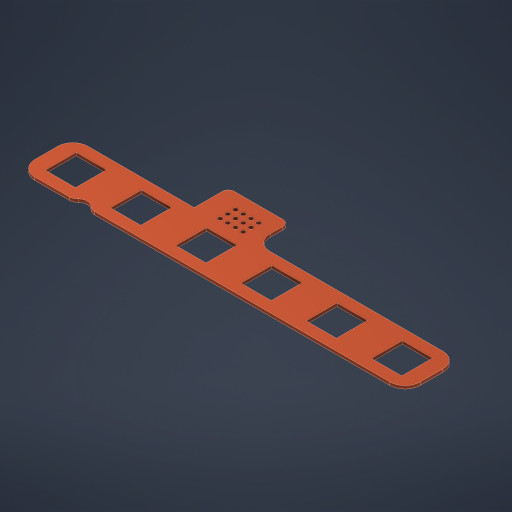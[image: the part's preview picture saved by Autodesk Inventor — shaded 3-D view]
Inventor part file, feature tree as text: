
AUTODESK INVENTOR PART (.ipt)
format: ipt  version: 2024.3 (Build 283343010, 343A)  size: 336,896 bytes
history: native  units: mm
features: fillet x4, sketch x2, extrude x1, hole x1, projected_geometry x1
ambient origin geometry x8: Origin, YZ Plane, XZ Plane, XY Plane, X Axis, Y Axis, Z Axis, Center Point
bodies: Volumenkörper1 (feature_tree)
feature tree (9):
  sketch  "Skizze1"  dims[d0=127.0mm d1=37.5mm d2=10.2mm]
  extrude  "Extrusion1"  Depth=10.2mm
  fillet  "Rundung1"  Radius=10.2mm
  hole  "Bohrung1"  [1 undecoded]
  fillet  "Rundung2"  Radius=5.75mm
  fillet  "Rundung3"  Radius=1.0mm
  fillet  "Rundung4"  Radius=5.0mm
  sketch  "Skizze2"  dims[d3=10.0mm d4=20.0mm d6=20.0mm d7=60.0mm d9=21.5mm d13=5.75mm d14=1.0mm d15=0.0mm d16=5.0mm d17=43.0mm d18=21.5mm d19=28.75mm d20=60.0mm d21=5.0mm d22=20.0mm d24=5.0mm d25=1.4mm d26=12.0mm d27=4.0mm d28=2.0mm d29=90.0deg d30=8.0mm d31=20.594885mm d32=2.0mm d33=5.0mm d34=40.0mm d36=2.54mm d37=30.0mm d39=2.54mm d43=3.0mm d44=1.25mm d45=10.75mm d46=3.0mm d48=8.75mm d49=8.75mm d50=5.0mm]
  projected_geometry  "Projizierte Kontur1"
note: 1 required parameter value undecoded (feature->parameter linkage not recoverable at this tier; creation-order binding heuristic only, values carry confidence <= 0.55)
